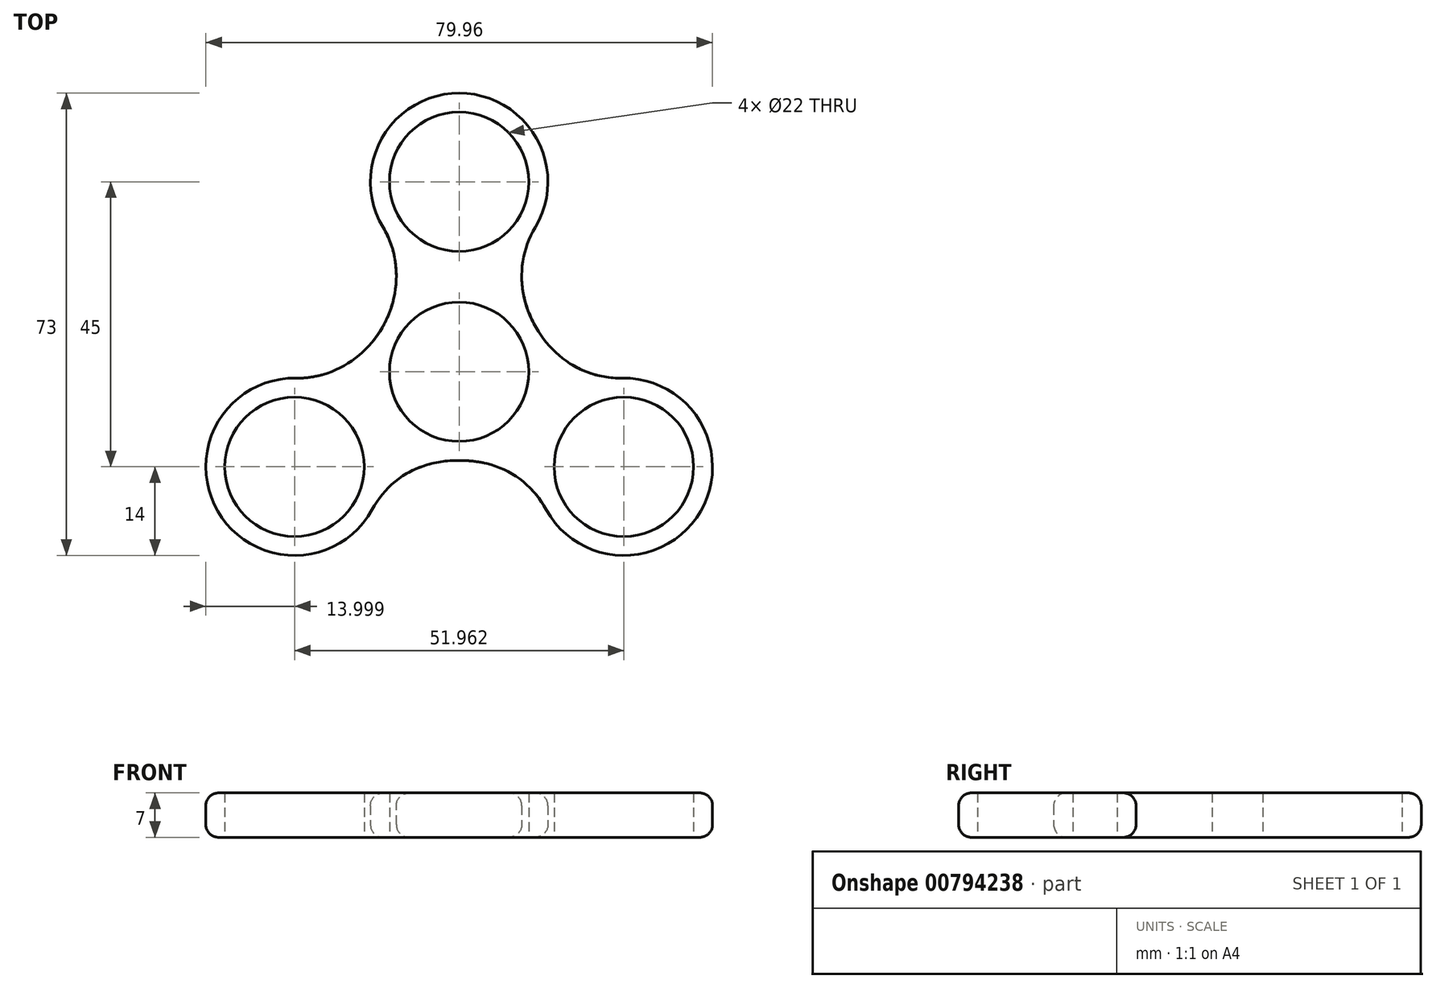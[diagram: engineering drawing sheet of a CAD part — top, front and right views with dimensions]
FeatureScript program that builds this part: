
annotation { "Feature Type Name" : "Feature", "Feature Type Description" : "" }
export const myFeature = defineFeature(function(context is Context, id is Id, definition is map)
    precondition{}
    {
        {
            var Q0;
            Q0=qCreatedBy(makeId("Top.planeOp"),FACE);
            var sketch = newSketch(context, id + "F0", { "sketchPlane" : qUnion([Q0])});
            skCircle(sketch, "E0", {"center": v(0, 0) * mm, "radius": 11 * mm});
            skLineSegment(sketch, "E1", {"start": v(0, 0) * mm, "end": v(0, 30) * mm});
            skLineSegment(sketch, "E2", {"start": v(0, 0) * mm, "end": v(-25.98, -15) * mm});
            skLineSegment(sketch, "E3", {"start": v(0, 0) * mm, "end": v(25.98, -15) * mm});
            skCircle(sketch, "E4", {"center": v(0, 30) * mm, "radius": 11 * mm});
            skCircle(sketch, "E5", {"center": v(-25.98, -15) * mm, "radius": 11 * mm});
            skCircle(sketch, "E6", {"center": v(25.98, -15) * mm, "radius": 11 * mm});
            skCircle(sketch, "E7", {"center": v(0, 30) * mm, "radius": 14 * mm});
            skCircle(sketch, "E8", {"center": v(-25.98, -15) * mm, "radius": 14 * mm});
            skCircle(sketch, "E9", {"center": v(25.98, -15) * mm, "radius": 14 * mm});
            skCircle(sketch, "E10", {"center": v(0, 0) * mm, "radius": 14 * mm});
            skFitSpline(sketch, "E11", {"points": [v(-12, 22.79) * mm, v(-12.12, 7) * mm, v(-25.74, -1) * mm], "startDerivative": vector(17.8, -29.61) * mm, "endDerivative": vector(-34.54, 0.6) * mm});
            skFitSpline(sketch, "E12", {"points": [v(12, 22.79) * mm, v(12.12, 7) * mm, v(25.74, -1) * mm], "startDerivative": vector(-18.84, -31.34) * mm, "endDerivative": vector(36.56, 0.64) * mm});
            skFitSpline(sketch, "E13", {"points": [v(-13.74, -21.79) * mm, v(0, -14) * mm, v(13.74, -21.79) * mm], "startDerivative": vector(19.42, 35.04) * mm, "endDerivative": vector(19.42, -35.04) * mm});
            skSolve(sketch);
        }
        {
            var Q0;
            Q0=makeQuery(id+"F0.imprint","IMPRINT",FACE,{"disambiguationData":[TD([[makeQuery(id+"F0.imprint","IMPRINT",EDGE,{"derivedFrom":sQuery(id+"F0.wireOp",EDGE,"E5")}),-1.0]])]});
            var Q1;
            {var subQ0=sQuery(id+"F0.wireOp",EDGE,"E2");var subQ1=sQuery(id+"F0.wireOp",EDGE,"E0");var subQ2=makeQuery(id+"F0.imprint","INTERSECT",VERTEX,{"derivedFrom":[subQ1,subQ0]});Q1=makeQuery(id+"F0.imprint","IMPRINT",FACE,{"disambiguationData":[TD([[makeQuery(id+"F0.imprint","IMPRINT",EDGE,{"disambiguationData":[TD([[subQ2,1.0]])],"derivedFrom":subQ1}),-1.0]])]});}
            var Q2;
            {var subQ0=sQuery(id+"F0.wireOp",EDGE,"E8");var subQ1=sQuery(id+"F0.wireOp",EDGE,"E2");var subQ2=makeQuery(id+"F0.imprint","INTERSECT",VERTEX,{"derivedFrom":[subQ1,subQ0]});Q2=makeQuery(id+"F0.imprint","IMPRINT",FACE,{"disambiguationData":[TD([[makeQuery(id+"F0.imprint","IMPRINT",EDGE,{"disambiguationData":[TD([[subQ2,1.0]])],"derivedFrom":subQ1}),-1.0]])]});}
            var Q3;
            {var subQ1=sQuery(id+"F0.wireOp",EDGE,"E0");var subQ6=sQuery(id+"F0.wireOp",EDGE,"E2");var subQ8=makeQuery(id+"F0.imprint","INTERSECT",VERTEX,{"derivedFrom":[subQ1,subQ6]});Q3=makeQuery(id+"F0.imprint","IMPRINT",FACE,{"disambiguationData":[TD([[makeQuery(id+"F0.imprint","IMPRINT",EDGE,{"disambiguationData":[TD([[subQ8,-1.0]])],"derivedFrom":subQ1}),-1.0]])]});}
            var Q4;
            {var subQ0=sQuery(id+"F0.wireOp",EDGE,"E8");var subQ1=sQuery(id+"F0.wireOp",EDGE,"E2");var subQ2=makeQuery(id+"F0.imprint","INTERSECT",VERTEX,{"derivedFrom":[subQ1,subQ0]});Q4=makeQuery(id+"F0.imprint","IMPRINT",FACE,{"disambiguationData":[TD([[makeQuery(id+"F0.imprint","IMPRINT",EDGE,{"disambiguationData":[TD([[subQ2,1.0]])],"derivedFrom":subQ1}),1.0]])]});}
            var Q5;
            {var subQ0=sQuery(id+"F0.wireOp",EDGE,"E9");var subQ1=sQuery(id+"F0.wireOp",EDGE,"E3");var subQ2=makeQuery(id+"F0.imprint","INTERSECT",VERTEX,{"derivedFrom":[subQ1,subQ0]});Q5=makeQuery(id+"F0.imprint","IMPRINT",FACE,{"disambiguationData":[TD([[makeQuery(id+"F0.imprint","IMPRINT",EDGE,{"disambiguationData":[TD([[subQ2,1.0]])],"derivedFrom":subQ1}),-1.0]])]});}
            var Q6;
            {var subQ1=sQuery(id+"F0.wireOp",EDGE,"E0");var subQ6=sQuery(id+"F0.wireOp",EDGE,"E1");var subQ8=makeQuery(id+"F0.imprint","INTERSECT",VERTEX,{"derivedFrom":[subQ1,subQ6]});Q6=makeQuery(id+"F0.imprint","IMPRINT",FACE,{"disambiguationData":[TD([[makeQuery(id+"F0.imprint","IMPRINT",EDGE,{"disambiguationData":[TD([[subQ8,1.0]])],"derivedFrom":subQ1}),-1.0]])]});}
            var Q7;
            Q7=makeQuery(id+"F0.imprint","IMPRINT",FACE,{"disambiguationData":[TD([[makeQuery(id+"F0.imprint","IMPRINT",EDGE,{"derivedFrom":sQuery(id+"F0.wireOp",EDGE,"E6")}),-1.0]])]});
            var Q8;
            {var subQ0=sQuery(id+"F0.wireOp",EDGE,"E9");var subQ1=sQuery(id+"F0.wireOp",EDGE,"E3");var subQ2=makeQuery(id+"F0.imprint","INTERSECT",VERTEX,{"derivedFrom":[subQ1,subQ0]});Q8=makeQuery(id+"F0.imprint","IMPRINT",FACE,{"disambiguationData":[TD([[makeQuery(id+"F0.imprint","IMPRINT",EDGE,{"disambiguationData":[TD([[subQ2,1.0]])],"derivedFrom":subQ1}),1.0]])]});}
            var Q9;
            {var subQ0=sQuery(id+"F0.wireOp",EDGE,"E7");var subQ1=sQuery(id+"F0.wireOp",EDGE,"E1");var subQ2=makeQuery(id+"F0.imprint","INTERSECT",VERTEX,{"derivedFrom":[subQ1,subQ0]});Q9=makeQuery(id+"F0.imprint","IMPRINT",FACE,{"disambiguationData":[TD([[makeQuery(id+"F0.imprint","IMPRINT",EDGE,{"disambiguationData":[TD([[subQ2,1.0]])],"derivedFrom":subQ1}),-1.0]])]});}
            var Q10;
            {var subQ0=sQuery(id+"F0.wireOp",EDGE,"E7");var subQ1=sQuery(id+"F0.wireOp",EDGE,"E1");var subQ2=makeQuery(id+"F0.imprint","INTERSECT",VERTEX,{"derivedFrom":[subQ1,subQ0]});Q10=makeQuery(id+"F0.imprint","IMPRINT",FACE,{"disambiguationData":[TD([[makeQuery(id+"F0.imprint","IMPRINT",EDGE,{"disambiguationData":[TD([[subQ2,1.0]])],"derivedFrom":subQ1}),1.0]])]});}
            var Q11;
            Q11=makeQuery(id+"F0.imprint","IMPRINT",FACE,{"disambiguationData":[TD([[makeQuery(id+"F0.imprint","IMPRINT",EDGE,{"derivedFrom":sQuery(id+"F0.wireOp",EDGE,"E4")}),-1.0]])]});
            extrude(context, id + "F1", {"entities" : qUnion([Q0, Q1, Q2, Q3, Q4, Q5, Q6, Q7, Q8, Q9, Q10, Q11]), "depth" : 7 * mm, "offsetDistance" : 25 * mm});
        }
        {
            var Q0;
            Q0=makeQuery(id+"F1.opExtrude","CAP_EDGE",EDGE,{"disambiguationData":[OSD([sQuery(id+"F0.wireOp",EDGE,"E8")])],"isStart":true});
            var Q1;
            Q1=makeQuery(id+"F1.opExtrude","CAP_EDGE",EDGE,{"disambiguationData":[OSD([sQuery(id+"F0.wireOp",EDGE,"E8")])],"isStart":false});
            fillet(context, id + "F2", {"entities" : qUnion([Q0, Q1]), "radius" : 2 * mm, "tangentPropagation" : true, "allowEdgeOverflow" : false});
        }
    });
